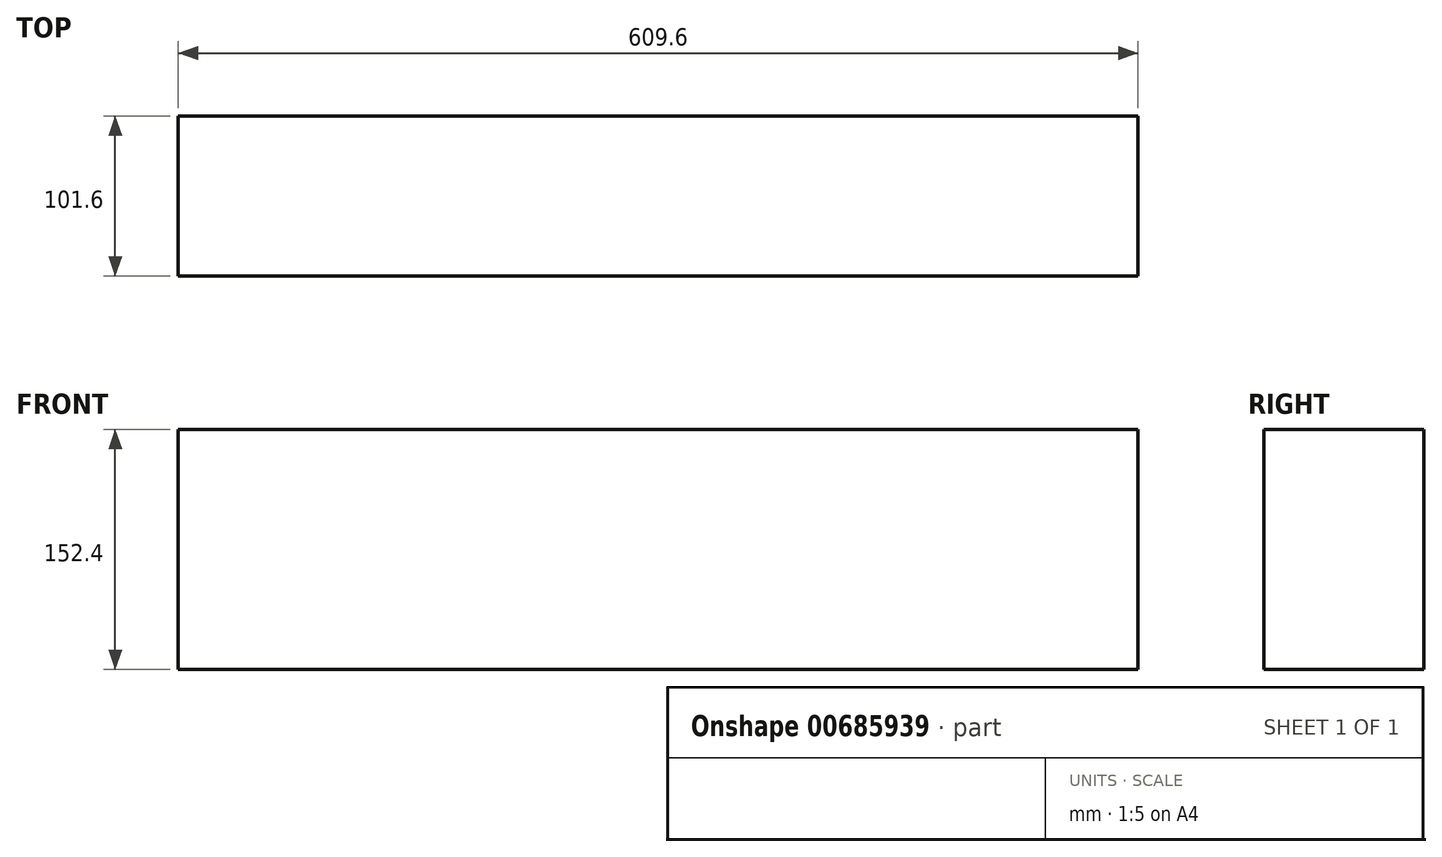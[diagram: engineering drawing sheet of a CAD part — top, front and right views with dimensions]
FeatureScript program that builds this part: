
annotation { "Feature Type Name" : "Feature", "Feature Type Description" : "" }
export const myFeature = defineFeature(function(context is Context, id is Id, definition is map)
    precondition{}
    {
        {
            var Q0;
            Q0=qCreatedBy(makeId("Top.planeOp"),FACE);
            var sketch = newSketch(context, id + "F0", { "sketchPlane" : qUnion([Q0])});
            skLineSegment(sketch, "E0.bottom", {"start": v(304.8, 50.8) * mm, "end": v(-304.8, 50.8) * mm});
            skLineSegment(sketch, "E0.top", {"start": v(304.8, -50.8) * mm, "end": v(-304.8, -50.8) * mm});
            skLineSegment(sketch, "E0.left", {"start": v(304.8, 50.8) * mm, "end": v(304.8, -50.8) * mm});
            skLineSegment(sketch, "E0.right", {"start": v(-304.8, 50.8) * mm, "end": v(-304.8, -50.8) * mm});
            skPoint(sketch, "E0.middle", {"position": v(0, 0) * mm});
            skSolve(sketch);
        }
        {
            var Q0;
            Q0=makeQuery(id+"F0.imprint","IMPRINT",FACE,{"disambiguationData":[TD([[makeQuery(id+"F0.imprint","IMPRINT",EDGE,{"derivedFrom":sQuery(id+"F0.wireOp",EDGE,"E0.bottom")}),1.0]])]});
            extrude(context, id + "F1", {"entities" : qUnion([Q0]), "depth" : 152.4 * mm, "offsetDistance" : 25.4 * mm});
        }
    });
